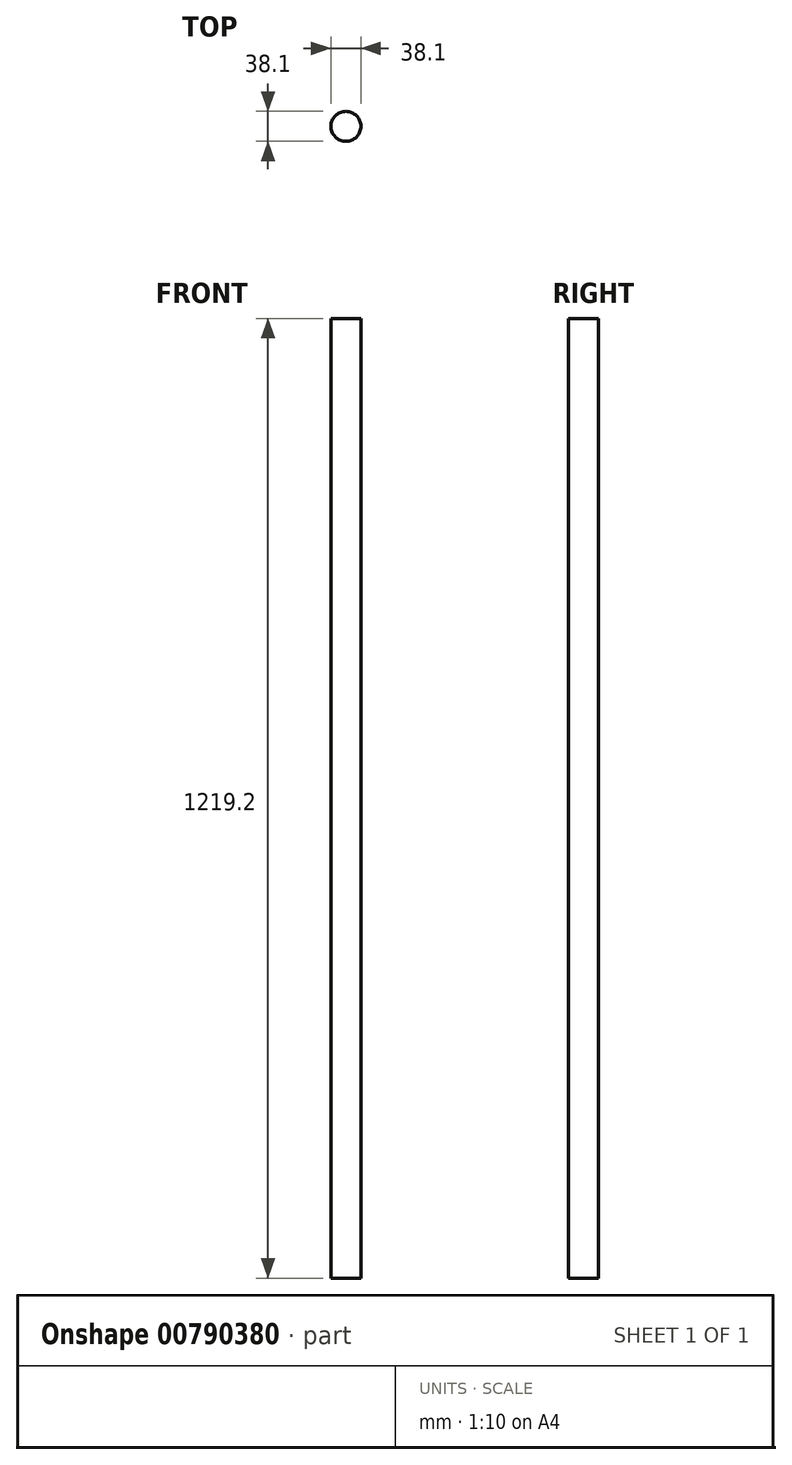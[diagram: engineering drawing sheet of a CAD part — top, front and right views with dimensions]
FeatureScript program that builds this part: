
annotation { "Feature Type Name" : "Feature", "Feature Type Description" : "" }
export const myFeature = defineFeature(function(context is Context, id is Id, definition is map)
    precondition{}
    {
        {
            var Q0;
            Q0=qCreatedBy(makeId("Top.planeOp"),FACE);
            var sketch = newSketch(context, id + "F0", { "sketchPlane" : qUnion([Q0])});
            skCircle(sketch, "E0", {"center": v(0, 0) * mm, "radius": 19.05 * mm});
            skSolve(sketch);
        }
        {
            var Q0;
            Q0=makeQuery(id+"F0.imprint","IMPRINT",FACE,{"disambiguationData":[TD([[makeQuery(id+"F0.imprint","IMPRINT",EDGE,{"derivedFrom":sQuery(id+"F0.wireOp",EDGE,"E0")}),1.0]])]});
            extrude(context, id + "F1", {"entities" : qUnion([Q0]), "depth" : 1219.2 * mm, "offsetDistance" : 25.4 * mm});
        }
    });
